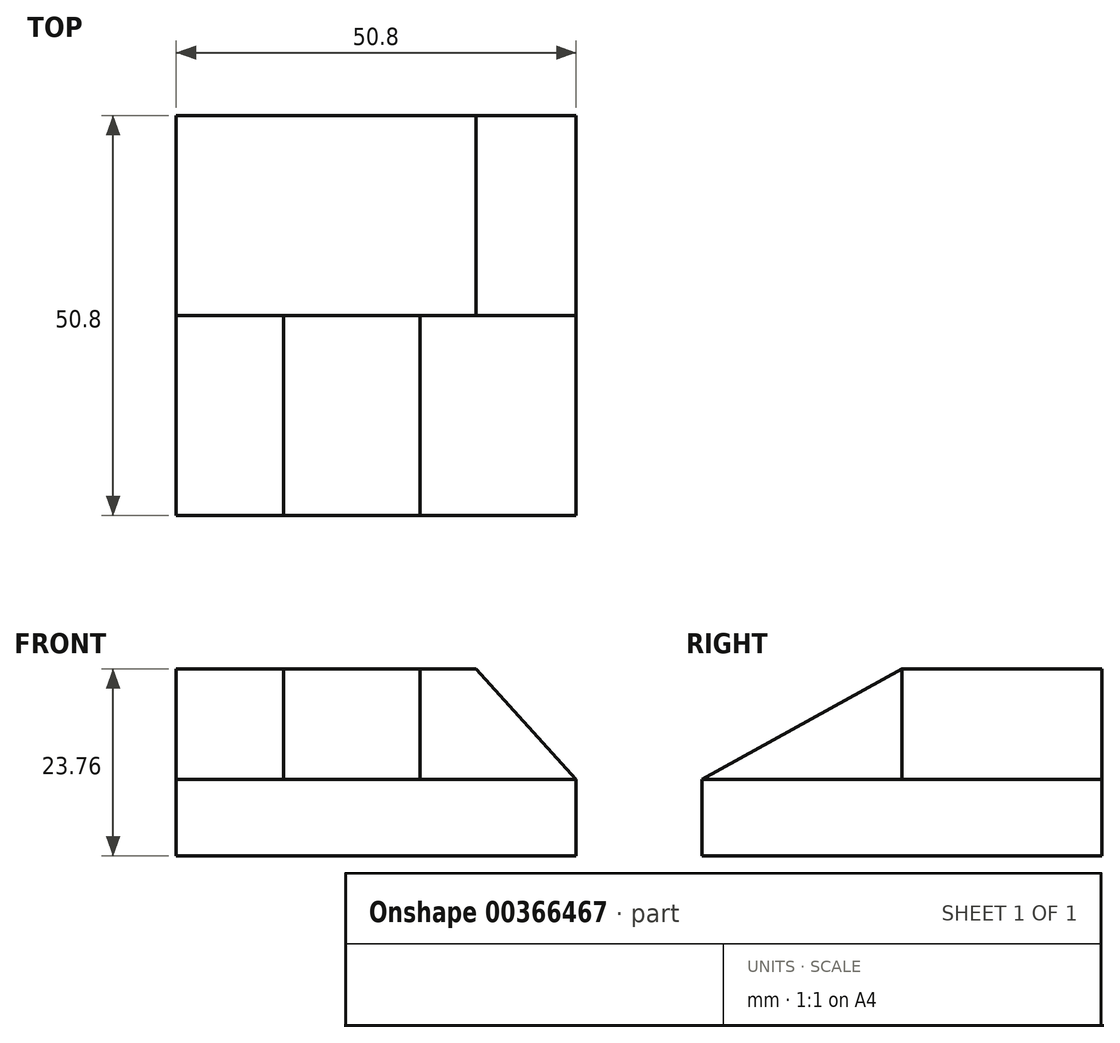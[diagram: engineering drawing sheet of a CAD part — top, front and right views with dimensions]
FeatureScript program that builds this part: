
annotation { "Feature Type Name" : "Feature", "Feature Type Description" : "" }
export const myFeature = defineFeature(function(context is Context, id is Id, definition is map)
    precondition{}
    {
        {
            var Q0;
            Q0=qCreatedBy(makeId("Front.planeOp"),FACE);
            var sketch = newSketch(context, id + "F0", { "sketchPlane" : qUnion([Q0])});
            skLineSegment(sketch, "E0", {"start": v(0, 0) * mm, "end": v(0, 23.76) * mm});
            skLineSegment(sketch, "E1", {"start": v(0, 23.76) * mm, "end": v(38.1, 23.76) * mm});
            skLineSegment(sketch, "E2", {"start": v(38.1, 23.76) * mm, "end": v(50.8, 9.73) * mm});
            skLineSegment(sketch, "E3", {"start": v(50.8, 9.73) * mm, "end": v(50.8, 0) * mm});
            skLineSegment(sketch, "E4", {"start": v(50.8, 0) * mm, "end": v(0, 0) * mm});
            skSolve(sketch);
        }
        {
            var Q0;
            Q0=makeQuery(id+"F0.imprint","IMPRINT",FACE,{"disambiguationData":[TD([[makeQuery(id+"F0.imprint","IMPRINT",EDGE,{"derivedFrom":sQuery(id+"F0.wireOp",EDGE,"E0")}),-1.0]])]});
            extrude(context, id + "F1", {"entities" : qUnion([Q0]), "depth" : 25.4 * mm});
        }
        {
            var Q0;
            Q0=makeQuery(id+"F1.opExtrude","CAP_FACE",FACE,{"disambiguationData":[OSD([sQuery(id+"F0.wireOp",EDGE,"E0"),sQuery(id+"F0.wireOp",EDGE,"E1"),sQuery(id+"F0.wireOp",EDGE,"E2"),sQuery(id+"F0.wireOp",EDGE,"E3"),sQuery(id+"F0.wireOp",EDGE,"E4")])],"isStart":false});
            var sketch = newSketch(context, id + "F2", { "sketchPlane" : qUnion([Q0])});
            skLineSegment(sketch, "E5", {"start": v(0, 0) * mm, "end": v(50.8, 0) * mm});
            skLineSegment(sketch, "E6", {"start": v(50.8, 0) * mm, "end": v(50.8, 9.73) * mm});
            skLineSegment(sketch, "E7", {"start": v(50.8, 9.73) * mm, "end": v(0, 9.73) * mm});
            skLineSegment(sketch, "E8", {"start": v(0, 9.73) * mm, "end": v(0, 0) * mm});
            skSolve(sketch);
        }
        {
            var Q0;
            Q0=makeQuery(id+"F2.imprint","IMPRINT",FACE,{"disambiguationData":[TD([[makeQuery(id+"F2.imprint","IMPRINT",EDGE,{"derivedFrom":sQuery(id+"F2.wireOp",EDGE,"E5")}),-1.0]])]});
            extrude(context, id + "F3", {"entities" : qUnion([Q0]), "operationType" : NewBodyOperationType.ADD, "depth" : 25.4 * mm});
        }
        {
            var Q0;
            Q0=makeQuery(id+"F1.opExtrude","CAP_FACE",FACE,{"disambiguationData":[OSD([sQuery(id+"F0.wireOp",EDGE,"E0"),sQuery(id+"F0.wireOp",EDGE,"E1"),sQuery(id+"F0.wireOp",EDGE,"E2"),sQuery(id+"F0.wireOp",EDGE,"E3"),sQuery(id+"F0.wireOp",EDGE,"E4")])],"isStart":false});
            var sketch = newSketch(context, id + "F4", { "sketchPlane" : qUnion([Q0])});
            skLineSegment(sketch, "E9", {"start": v(13.62, 23.76) * mm, "end": v(13.62, 9.73) * mm});
            skLineSegment(sketch, "E10", {"start": v(13.62, 9.73) * mm, "end": v(30.95, 9.73) * mm});
            skLineSegment(sketch, "E11", {"start": v(30.95, 9.73) * mm, "end": v(30.95, 23.76) * mm});
            skLineSegment(sketch, "E12", {"start": v(30.95, 23.76) * mm, "end": v(13.62, 23.76) * mm});
            skSolve(sketch);
        }
        {
            var Q0;
            Q0=makeQuery(id+"F4.imprint","IMPRINT",FACE,{"disambiguationData":[TD([[makeQuery(id+"F4.imprint","IMPRINT",EDGE,{"derivedFrom":sQuery(id+"F4.wireOp",EDGE,"E9")}),1.0]])]});
            extrude(context, id + "F5", {"entities" : qUnion([Q0]), "operationType" : NewBodyOperationType.ADD, "depth" : 25.4 * mm});
        }
        {
            var Q0;
            Q0=makeQuery(id+"F5.opExtrude","SWEPT_FACE",FACE,{"disambiguationData":[OSD([sQuery(id+"F4.wireOp",EDGE,"E11")])]});
            var sketch = newSketch(context, id + "F6", { "sketchPlane" : qUnion([Q0])});
            skLineSegment(sketch, "E13", {"start": v(-50.8, 9.73) * mm, "end": v(-25.4, 23.76) * mm});
            skSolve(sketch);
        }
        {
            var Q0;
            Q0=makeQuery(id+"F6.imprint","IMPRINT",FACE,{"disambiguationData":[TD([[makeQuery(id+"F6.imprint","IMPRINT",EDGE,{"derivedFrom":sQuery(id+"F6.wireOp",EDGE,"E13")}),1.0]])]});
            extrude(context, id + "F7", {"entities" : qUnion([Q0]), "operationType" : NewBodyOperationType.REMOVE, "oppositeDirection" : true, "depth" : 25.4 * mm});
        }
    });
